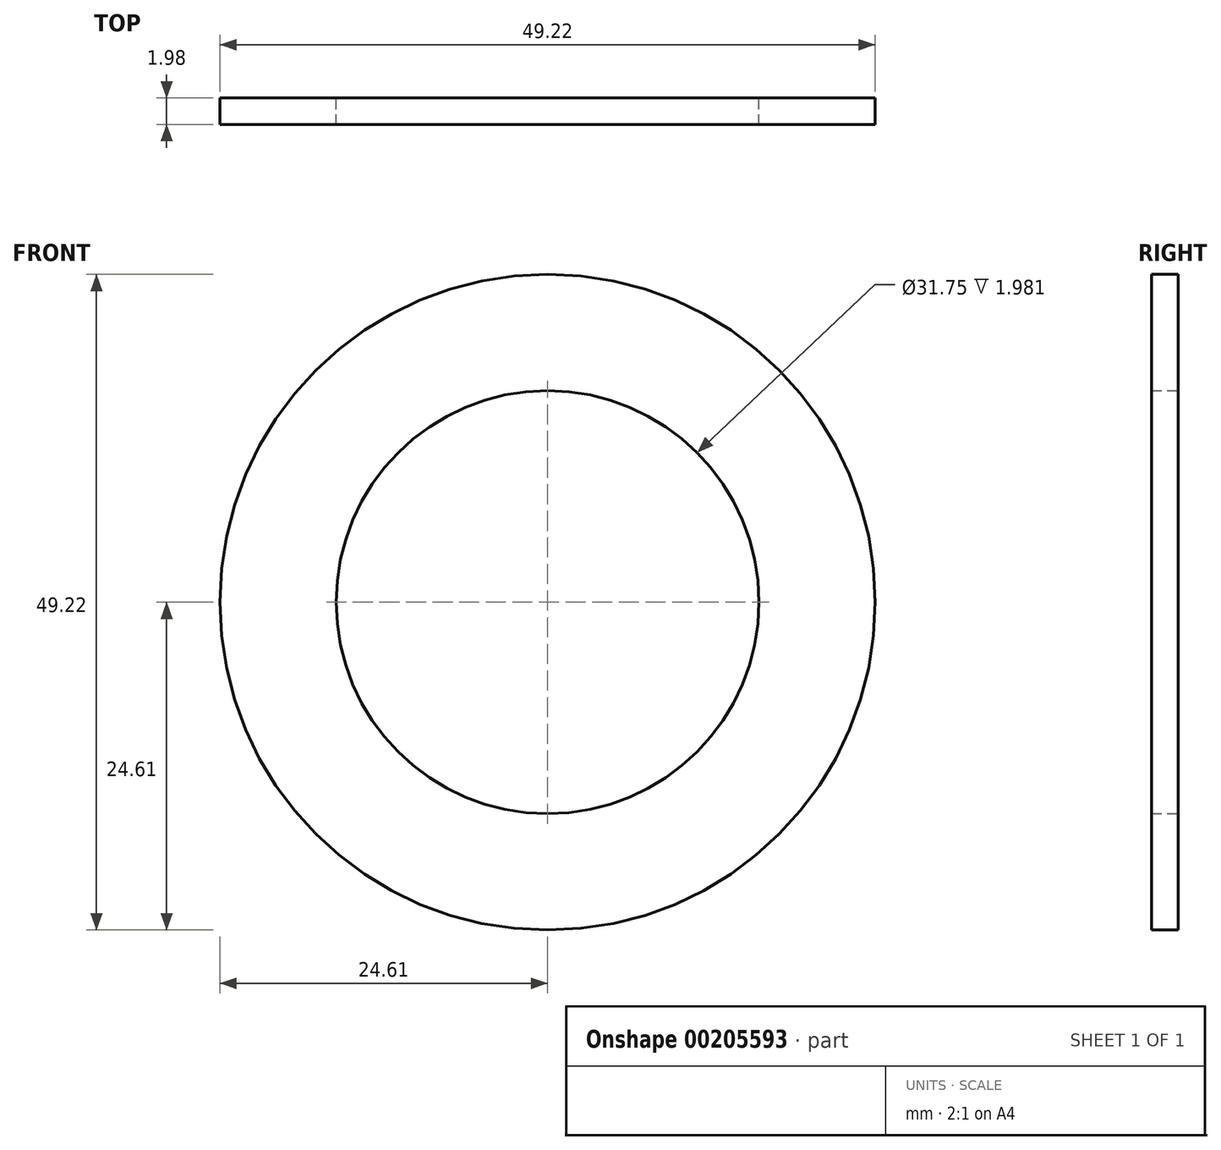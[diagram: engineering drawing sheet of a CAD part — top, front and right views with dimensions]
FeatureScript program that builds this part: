
annotation { "Feature Type Name" : "Feature", "Feature Type Description" : "" }
export const myFeature = defineFeature(function(context is Context, id is Id, definition is map)
    precondition{}
    {
        {
            var Q0;
            Q0=qCreatedBy(makeId("Front.planeOp"),FACE);
            var sketch = newSketch(context, id + "F0", { "sketchPlane" : qUnion([Q0])});
            skCircle(sketch, "E0", {"center": v(0, 0) * mm, "radius": 15.88 * mm});
            skCircle(sketch, "E1", {"center": v(0, 0) * mm, "radius": 24.61 * mm});
            skSolve(sketch);
        }
        {
            var Q0;
            Q0=qSketchRegion(id+"F0",true);
            extrude(context, id + "F1", {"entities" : qUnion([Q0]), "depth" : 1.98 * mm});
        }
    });
